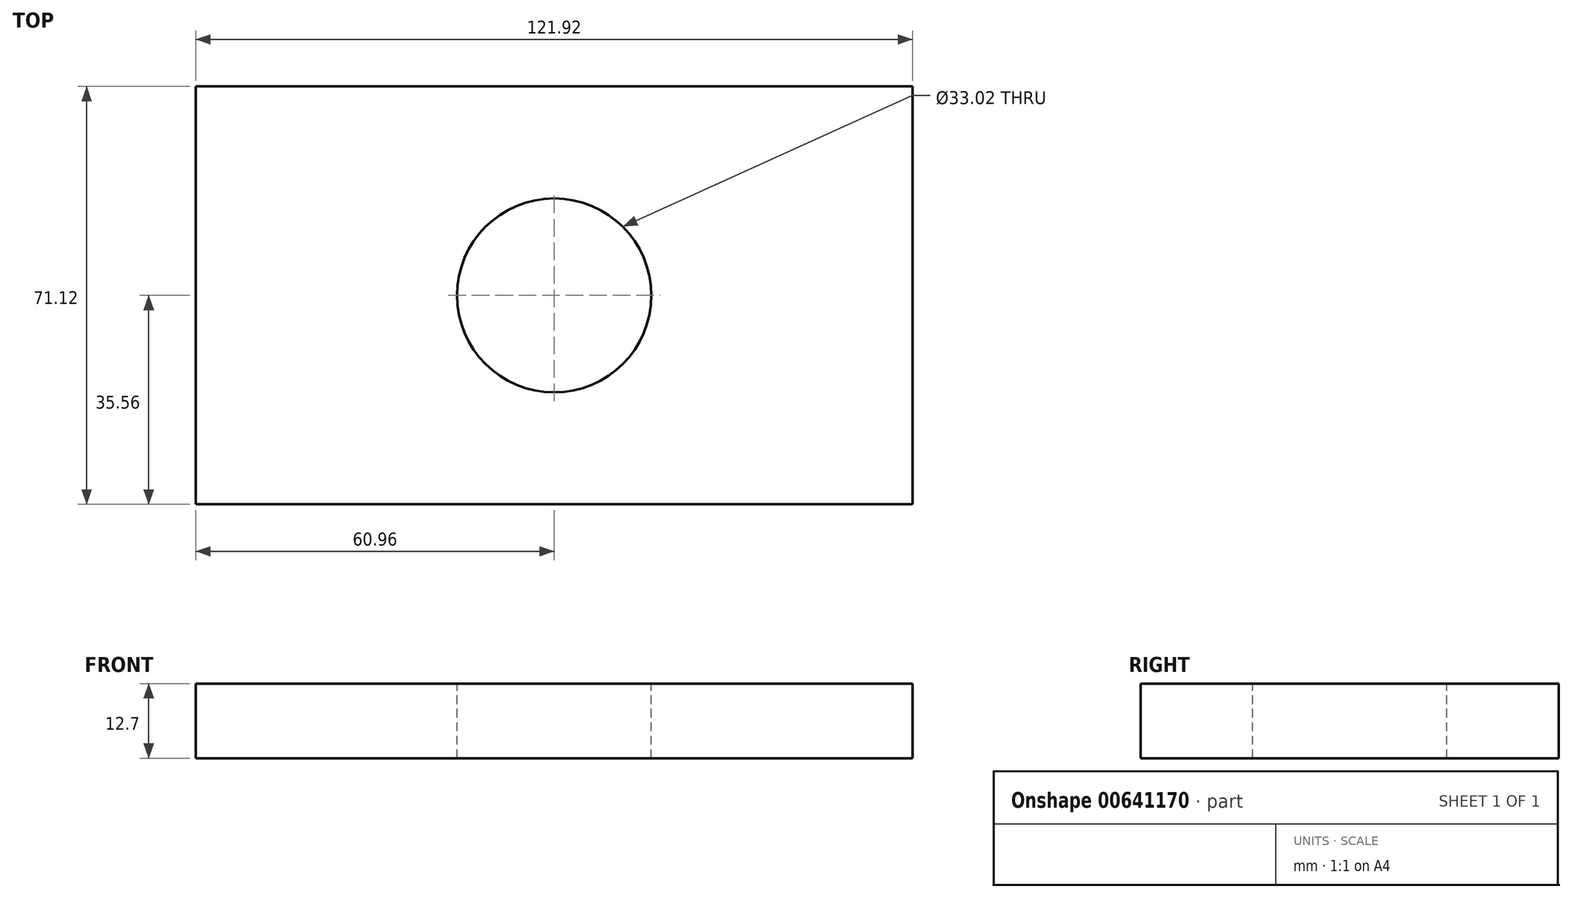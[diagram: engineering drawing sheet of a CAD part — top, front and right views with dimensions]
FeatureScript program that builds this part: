
annotation { "Feature Type Name" : "Feature", "Feature Type Description" : "" }
export const myFeature = defineFeature(function(context is Context, id is Id, definition is map)
    precondition{}
    {
        {
            var Q0;
            Q0=qCreatedBy(makeId("Top.planeOp"),FACE);
            var sketch = newSketch(context, id + "F0", { "sketchPlane" : qUnion([Q0])});
            skLineSegment(sketch, "E0.bottom", {"start": v(-60.96, -35.56) * mm, "end": v(60.96, -35.56) * mm});
            skLineSegment(sketch, "E0.top", {"start": v(-60.96, 35.56) * mm, "end": v(60.96, 35.56) * mm});
            skLineSegment(sketch, "E0.left", {"start": v(-60.96, -35.56) * mm, "end": v(-60.96, 35.56) * mm});
            skLineSegment(sketch, "E0.right", {"start": v(60.96, -35.56) * mm, "end": v(60.96, 35.56) * mm});
            skPoint(sketch, "E0.middle", {"position": v(0, 0) * mm});
            skCircle(sketch, "E1", {"center": v(0, 0) * mm, "radius": 16.51 * mm});
            skSolve(sketch);
        }
        {
            var Q0;
            Q0=makeQuery(id+"F0.imprint","IMPRINT",FACE,{"disambiguationData":[TD([[makeQuery(id+"F0.imprint","IMPRINT",EDGE,{"derivedFrom":sQuery(id+"F0.wireOp",EDGE,"E0.bottom")}),1.0]])]});
            extrude(context, id + "F1", {"entities" : qUnion([Q0]), "oppositeDirection" : true, "depth" : 12.7 * mm, "offsetDistance" : 25.4 * mm});
        }
    });
